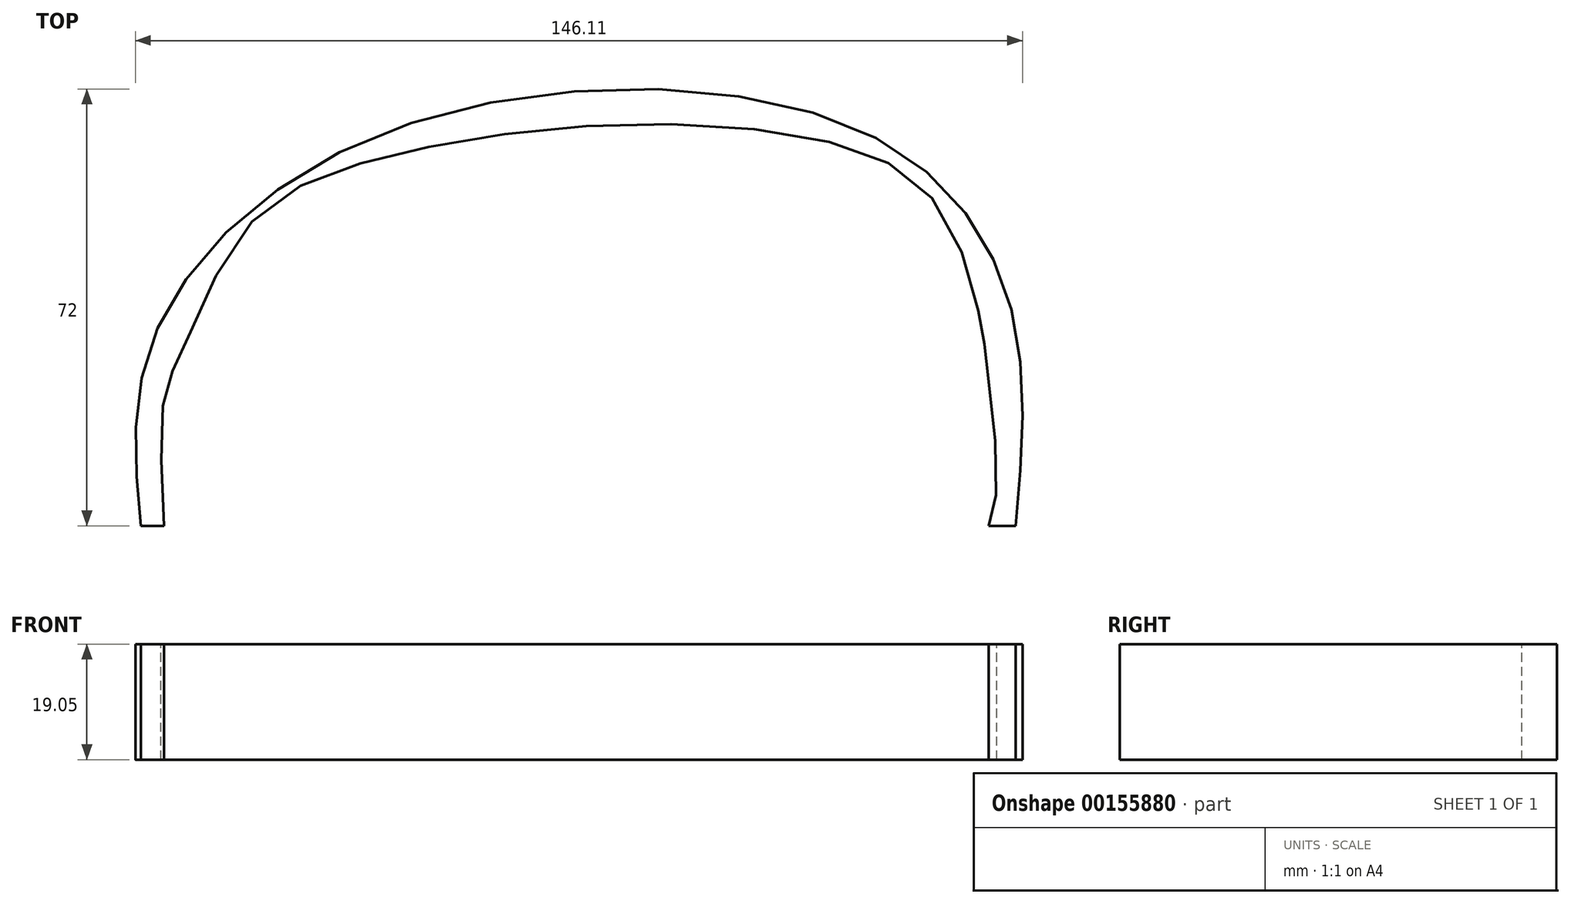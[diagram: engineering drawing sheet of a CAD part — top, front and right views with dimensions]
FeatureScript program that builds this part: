
annotation { "Feature Type Name" : "Feature", "Feature Type Description" : "" }
export const myFeature = defineFeature(function(context is Context, id is Id, definition is map)
    precondition{}
    {
        {
            var Q0;
            Q0=qCreatedBy(makeId("Top.planeOp"),FACE);
            var sketch = newSketch(context, id + "F0", { "sketchPlane" : qUnion([Q0])});
            skLineSegment(sketch, "E0.bottom", {"start": v(-76.2, 76.08) * mm, "end": v(76.2, 76.08) * mm});
            skLineSegment(sketch, "E0.top", {"start": v(-76.2, -76.08) * mm, "end": v(76.2, -76.08) * mm});
            skLineSegment(sketch, "E0.left", {"start": v(-76.2, 76.08) * mm, "end": v(-76.2, -76.08) * mm});
            skLineSegment(sketch, "E0.right", {"start": v(76.2, 76.08) * mm, "end": v(76.2, -76.08) * mm});
            skPoint(sketch, "E0.middle", {"position": v(0, 0) * mm});
            skSolve(sketch);
        }
        {
            var Q0;
            Q0 = qSketchRegion(id + "F0", true);
            extrude(context, id + "F1", {"entities" : qUnion([Q0]), "depth" : 19.05 * mm});
        }
        {
            var Q0;
            Q0=makeQuery(id+"F1.opExtrude","CAP_FACE",FACE,{"disambiguationData":[OSD([sQuery(id+"F0.wireOp",EDGE,"E0.bottom"),sQuery(id+"F0.wireOp",EDGE,"E0.top"),sQuery(id+"F0.wireOp",EDGE,"E0.left"),sQuery(id+"F0.wireOp",EDGE,"E0.right")])],"isStart":false});
            var sketch = newSketch(context, id + "F2", { "sketchPlane" : qUnion([Q0])});
            skFitSpline(sketch, "E1", {"points": [v(-68.58, -76.08) * mm, v(-68.58, -54.84) * mm, v(-65.58, -47.22) * mm, v(-54.73, -26.67) * mm, v(-33.48, -15.59) * mm, v(3.93, -10.04) * mm, v(43.64, -13.5) * mm, v(60.27, -25.52) * mm, v(66.27, -44.45) * mm, v(66.73, -48.14) * mm, v(68.58, -68.7) * mm, v(67.2, -76.08) * mm], "startDerivative": vector(-13.78, 256.86) * mm, "endDerivative": vector(-34.43, -99.26) * mm});
            skSolve(sketch);
        }
        {
            var Q0;
            Q0 = qSketchRegion(id + "F2", true);
            var Q1;
            {var subQ0=sQuery(id+"F2.wireOp",EDGE,"E1");Q1=makeQuery(id+"F2.imprint","IMPRINT",FACE,{"disambiguationData":[TD([[makeQuery(id+"F2.imprint","IMPRINT",EDGE,{"derivedFrom":subQ0}),-1.0]])]});}
            extrude(context, id + "F3", {"entities" : qUnion([Q0, Q1]), "operationType" : NewBodyOperationType.REMOVE, "oppositeDirection" : true, "depth" : 25.4 * mm});
        }
        {
            var Q0;
            Q0=makeQuery(id+"F1.opExtrude","CAP_FACE",FACE,{"disambiguationData":[OSD([sQuery(id+"F0.wireOp",EDGE,"E0.bottom"),sQuery(id+"F0.wireOp",EDGE,"E0.top"),sQuery(id+"F0.wireOp",EDGE,"E0.left"),sQuery(id+"F0.wireOp",EDGE,"E0.right")])],"isStart":false});
            var sketch = newSketch(context, id + "F4", { "sketchPlane" : qUnion([Q0])});
            skLineSegment(sketch, "E2", {"start": v(-76.2, 0) * mm, "end": v(76.2, 0) * mm});
            skSolve(sketch);
        }
        {
            var Q0;
            Q0 = qSketchRegion(id + "F4", true);
            var Q1;
            {var subQ0=sQuery(id+"F4.wireOp",EDGE,"E2");Q1=makeQuery(id+"F4.imprint","IMPRINT",FACE,{"disambiguationData":[TD([[makeQuery(id+"F4.imprint","IMPRINT",EDGE,{"derivedFrom":subQ0}),1.0]])]});}
            extrude(context, id + "F5", {"entities" : qUnion([Q0, Q1]), "operationType" : NewBodyOperationType.REMOVE, "oppositeDirection" : true, "depth" : 25.4 * mm});
        }
        {
            var Q0;
            Q0=makeQuery(id+"F1.opExtrude","CAP_FACE",FACE,{"disambiguationData":[OSD([sQuery(id+"F0.wireOp",EDGE,"E0.bottom"),sQuery(id+"F0.wireOp",EDGE,"E0.top"),sQuery(id+"F0.wireOp",EDGE,"E0.left"),sQuery(id+"F0.wireOp",EDGE,"E0.right")])],"isStart":false});
            var sketch = newSketch(context, id + "F6", { "sketchPlane" : qUnion([Q0])});
            skFitSpline(sketch, "E3", {"points": [v(-76.2, -46.07) * mm, v(-67.89, -27.82) * mm, v(-50.34, -12.82) * mm, v(-18.01, -3.81) * mm, v(32.79, -4.04) * mm, v(66.73, -18.82) * mm, v(76.2, -45.84) * mm], "startDerivative": vector(50.1, 142.55) * mm, "endDerivative": vector(31.37, -187.64) * mm});
            skSolve(sketch);
        }
        {
            var Q0;
            Q0 = qSketchRegion(id + "F6", true);
            var Q1;
            {var subQ0=sQuery(id+"F6.wireOp",EDGE,"E3");Q1=makeQuery(id+"F6.imprint","IMPRINT",FACE,{"disambiguationData":[TD([[makeQuery(id+"F6.imprint","IMPRINT",EDGE,{"derivedFrom":subQ0}),1.0]])]});}
            extrude(context, id + "F7", {"entities" : qUnion([Q0, Q1]), "operationType" : NewBodyOperationType.REMOVE, "oppositeDirection" : true, "depth" : 25.4 * mm});
        }
        {
            var Q0;
            Q0=makeQuery(id+"F1.opExtrude","CAP_FACE",FACE,{"disambiguationData":[OSD([sQuery(id+"F0.wireOp",EDGE,"E0.bottom"),sQuery(id+"F0.wireOp",EDGE,"E0.top"),sQuery(id+"F0.wireOp",EDGE,"E0.left"),sQuery(id+"F0.wireOp",EDGE,"E0.right")])],"isStart":false});
            var sketch = newSketch(context, id + "F8", { "sketchPlane" : qUnion([Q0])});
            skFitSpline(sketch, "E4", {"points": [v(-72.4, -76.08) * mm, v(-70.43, -45.37) * mm, v(-32.1, -11.2) * mm, v(45.26, -10.5) * mm, v(70.66, -39.37) * mm, v(71.7, -76.08) * mm], "startDerivative": vector(-18.67, 186.55) * mm, "endDerivative": vector(-18.34, -210.16) * mm});
            skSolve(sketch);
        }
        {
            var Q0;
            Q0 = qSketchRegion(id + "F8", true);
            var Q1;
            {var subQ4=sQuery(id+"F8.wireOp",EDGE,"E4");Q1=makeQuery(id+"F8.imprint","IMPRINT",FACE,{"disambiguationData":[TD([[makeQuery(id+"F8.imprint","IMPRINT",EDGE,{"derivedFrom":subQ4}),1.0]])]});}
            extrude(context, id + "F9", {"entities" : qUnion([Q0, Q1]), "operationType" : NewBodyOperationType.REMOVE, "oppositeDirection" : true, "depth" : 25.4 * mm});
        }
    });
